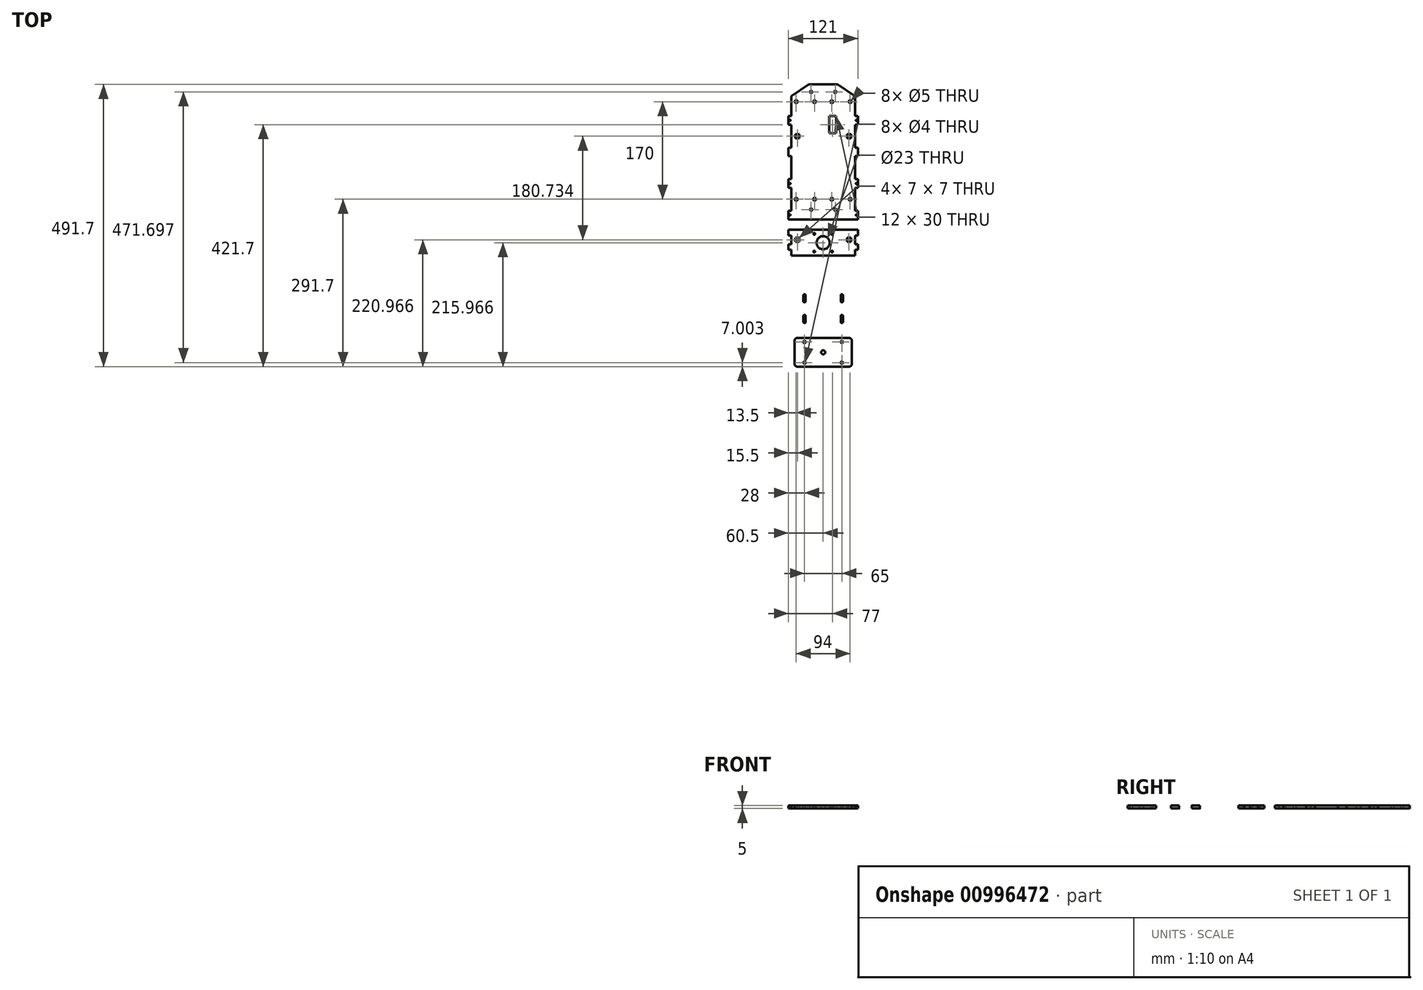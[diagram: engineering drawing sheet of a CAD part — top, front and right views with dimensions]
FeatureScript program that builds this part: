
annotation { "Feature Type Name" : "Feature", "Feature Type Description" : "" }
export const myFeature = defineFeature(function(context is Context, id is Id, definition is map)
    precondition{}
    {
        {
            var Q0;
            Q0=qCreatedBy(makeId("Top.planeOp"),FACE);
            var sketch = newSketch(context, id + "F0", { "sketchPlane" : qUnion([Q0])});
            skLineSegment(sketch, "E0.bottom", {"start": v(-55.5, 107.5) * mm, "end": v(55.5, 107.5) * mm, "construction": true});
            skLineSegment(sketch, "E0.top", {"start": v(-55.5, -107.5) * mm, "end": v(55.5, -107.5) * mm});
            skLineSegment(sketch, "E0.left", {"start": v(-55.5, 107.5) * mm, "end": v(-55.5, 72.5) * mm});
            skLineSegment(sketch, "E0.right", {"start": v(55.5, 107.5) * mm, "end": v(55.5, 72.5) * mm});
            skLineSegment(sketch, "E1", {"start": v(-55.5, 0) * mm, "end": v(55.5, 0) * mm, "construction": true});
            skLineSegment(sketch, "E2", {"start": v(0, 107.5) * mm, "end": v(0, -107.5) * mm, "construction": true});
            skLineSegment(sketch, "E3", {"start": v(-55.5, 107.5) * mm, "end": v(-25.5, 127.5) * mm});
            skLineSegment(sketch, "E4", {"start": v(-25.5, 127.5) * mm, "end": v(25.5, 127.5) * mm});
            skLineSegment(sketch, "E5", {"start": v(25.5, 127.5) * mm, "end": v(55.5, 107.5) * mm});
            skLineSegment(sketch, "E6.bottom", {"start": v(-55.5, -107.5) * mm, "end": v(-60.5, -107.5) * mm});
            skLineSegment(sketch, "E6.top", {"start": v(-55.5, -92.5) * mm, "end": v(-60.5, -92.5) * mm});
            skLineSegment(sketch, "E6.right", {"start": v(-60.5, -107.5) * mm, "end": v(-60.5, -92.5) * mm});
            skLineSegment(sketch, "E7.MirrorCS", {"start": v(55.5, -92.5) * mm, "end": v(60.5, -92.5) * mm});
            skLineSegment(sketch, "E8.MirrorCS", {"start": v(60.5, -107.5) * mm, "end": v(60.5, -92.5) * mm});
            skLineSegment(sketch, "E9.MirrorCS", {"start": v(55.5, -107.5) * mm, "end": v(60.5, -107.5) * mm});
            skLineSegment(sketch, "E10.bottom", {"start": v(-55.5, -52.5) * mm, "end": v(-60.5, -52.5) * mm});
            skLineSegment(sketch, "E10.top", {"start": v(-55.5, -37.5) * mm, "end": v(-60.5, -37.5) * mm});
            skLineSegment(sketch, "E10.right", {"start": v(-60.5, -52.5) * mm, "end": v(-60.5, -37.5) * mm});
            skLineSegment(sketch, "E11.bottom", {"start": v(-55.5, 2.5) * mm, "end": v(-60.5, 2.5) * mm});
            skLineSegment(sketch, "E11.top", {"start": v(-55.5, 17.5) * mm, "end": v(-60.5, 17.5) * mm});
            skLineSegment(sketch, "E11.right", {"start": v(-60.5, 2.5) * mm, "end": v(-60.5, 17.5) * mm});
            skLineSegment(sketch, "E12.bottom", {"start": v(-55.5, 57.5) * mm, "end": v(-60.5, 57.5) * mm});
            skLineSegment(sketch, "E12.top", {"start": v(-55.5, 72.5) * mm, "end": v(-60.5, 72.5) * mm});
            skLineSegment(sketch, "E12.right", {"start": v(-60.5, 57.5) * mm, "end": v(-60.5, 72.5) * mm});
            skLineSegment(sketch, "E13.MirrorCS", {"start": v(55.5, 72.5) * mm, "end": v(60.5, 72.5) * mm});
            skLineSegment(sketch, "E14.MirrorCS", {"start": v(60.5, 57.5) * mm, "end": v(60.5, 72.5) * mm});
            skLineSegment(sketch, "E15.MirrorCS", {"start": v(55.5, 57.5) * mm, "end": v(60.5, 57.5) * mm});
            skLineSegment(sketch, "E16.MirrorCS", {"start": v(55.5, 17.5) * mm, "end": v(60.5, 17.5) * mm});
            skLineSegment(sketch, "E17.MirrorCS", {"start": v(60.5, 2.5) * mm, "end": v(60.5, 17.5) * mm});
            skLineSegment(sketch, "E18.MirrorCS", {"start": v(55.5, 2.5) * mm, "end": v(60.5, 2.5) * mm});
            skLineSegment(sketch, "E19.MirrorCS", {"start": v(55.5, -37.5) * mm, "end": v(60.5, -37.5) * mm});
            skLineSegment(sketch, "E20.MirrorCS", {"start": v(60.5, -52.5) * mm, "end": v(60.5, -37.5) * mm});
            skLineSegment(sketch, "E21.MirrorCS", {"start": v(55.5, -52.5) * mm, "end": v(60.5, -52.5) * mm});
            skLineSegment(sketch, "E22.trimOffspring", {"start": v(55.5, 57.5) * mm, "end": v(55.5, 17.5) * mm});
            skLineSegment(sketch, "E23.trimOffspring", {"start": v(55.5, 2.5) * mm, "end": v(55.5, -37.5) * mm});
            skLineSegment(sketch, "E24.trimOffspring", {"start": v(55.5, -52.5) * mm, "end": v(55.5, -92.5) * mm});
            skLineSegment(sketch, "E25.trimOffspring", {"start": v(-55.5, -52.5) * mm, "end": v(-55.5, -92.5) * mm});
            skLineSegment(sketch, "E26.trimOffspring", {"start": v(-55.5, 2.5) * mm, "end": v(-55.5, -37.5) * mm});
            skLineSegment(sketch, "E27.trimOffspring", {"start": v(-55.5, 57.5) * mm, "end": v(-55.5, 17.5) * mm});
            skLineSegment(sketch, "E28.bottom", {"start": v(10.5, 72.5) * mm, "end": v(22.5, 72.5) * mm});
            skLineSegment(sketch, "E28.top", {"start": v(10.5, 42.5) * mm, "end": v(22.5, 42.5) * mm});
            skLineSegment(sketch, "E28.left", {"start": v(10.5, 72.5) * mm, "end": v(10.5, 42.5) * mm});
            skLineSegment(sketch, "E28.right", {"start": v(22.5, 72.5) * mm, "end": v(22.5, 42.5) * mm});
            skLineSegment(sketch, "E29.bottom", {"start": v(-48.5, 41) * mm, "end": v(-41.5, 41) * mm});
            skLineSegment(sketch, "E29.top", {"start": v(-48.5, 34) * mm, "end": v(-41.5, 34) * mm});
            skLineSegment(sketch, "E29.left", {"start": v(-48.5, 41) * mm, "end": v(-48.5, 34) * mm});
            skLineSegment(sketch, "E29.right", {"start": v(-41.5, 41) * mm, "end": v(-41.5, 34) * mm});
            skPoint(sketch, "E30", {"position": v(-48.5, 37.5) * mm});
            skPoint(sketch, "E31", {"position": v(-55.5, 37.5) * mm});
            skLineSegment(sketch, "E32.MirrorCS", {"start": v(41.5, 41) * mm, "end": v(41.5, 34) * mm});
            skLineSegment(sketch, "E33.MirrorCS", {"start": v(48.5, 41) * mm, "end": v(41.5, 41) * mm});
            skLineSegment(sketch, "E34.MirrorCS", {"start": v(48.5, 41) * mm, "end": v(48.5, 34) * mm});
            skLineSegment(sketch, "E35.MirrorCS", {"start": v(48.5, 34) * mm, "end": v(41.5, 34) * mm});
            skSolve(sketch);
        }
        {
            var Q0;
            Q0=makeQuery(id+"F0.imprint","IMPRINT",FACE,{"disambiguationData":[TD([[makeQuery(id+"F0.imprint","IMPRINT",EDGE,{"derivedFrom":sQuery(id+"F0.wireOp",EDGE,"E0.top")}),1.0]])]});
            extrude(context, id + "F1", {"entities" : qUnion([Q0]), "depth" : 5 * mm, "offsetDistance" : 25 * mm});
        }
        {
            var Q0;
            Q0=makeQuery(id+"F1.opExtrude","CAP_FACE",FACE,{"disambiguationData":[OSD([sQuery(id+"F0.wireOp",EDGE,"E0.bottom"),sQuery(id+"F0.wireOp",EDGE,"E0.top"),sQuery(id+"F0.wireOp",EDGE,"E0.left"),sQuery(id+"F0.wireOp",EDGE,"E0.right")])],"isStart":false});
            var sketch = newSketch(context, id + "F2", { "sketchPlane" : qUnion([Q0])});
            skPoint(sketch, "E36", {"position": v(-47, 97.5) * mm});
            skPoint(sketch, "E37", {"position": v(-15, 97.5) * mm});
            skPoint(sketch, "E38", {"position": v(-47, -72.5) * mm});
            skPoint(sketch, "E39", {"position": v(-15, -72.5) * mm});
            skLineSegment(sketch, "E40.bottom", {"start": v(-55.5, 107.5) * mm, "end": v(55.5, 107.5) * mm});
            skLineSegment(sketch, "E40.top", {"start": v(-55.5, 107.5) * mm, "end": v(55.5, 107.5) * mm});
            skLineSegment(sketch, "E40.left", {"start": v(-55.5, 107.5) * mm, "end": v(-55.5, 107.5) * mm});
            skLineSegment(sketch, "E40.right", {"start": v(55.5, 107.5) * mm, "end": v(55.5, 107.5) * mm});
            skLineSegment(sketch, "E41", {"start": v(0, 107.5) * mm, "end": v(0, 107.5) * mm});
            skPoint(sketch, "E42", {"position": v(15, 97.5) * mm});
            skPoint(sketch, "E43", {"position": v(47, 97.5) * mm});
            skPoint(sketch, "E44", {"position": v(47, -72.5) * mm});
            skPoint(sketch, "E45", {"position": v(15, -72.5) * mm});
            skLineSegment(sketch, "E46", {"start": v(-47, 97.5) * mm, "end": v(-15, 97.5) * mm, "construction": true});
            skLineSegment(sketch, "E47", {"start": v(15, 97.5) * mm, "end": v(47, 97.5) * mm, "construction": true});
            skPoint(sketch, "E48", {"position": v(-31, 97.5) * mm});
            skPoint(sketch, "E49", {"position": v(31, 97.5) * mm});
            skSolve(sketch);
        }
        {
            var Q0;
            Q0=sQuery(id+"F2.wireOp",VERTEX,"E36");
            var Q1;
            Q1=sQuery(id+"F2.wireOp",VERTEX,"E37");
            var Q2;
            Q2=sQuery(id+"F2.wireOp",VERTEX,"E42");
            var Q3;
            Q3=sQuery(id+"F2.wireOp",VERTEX,"E43");
            var Q4;
            Q4=sQuery(id+"F2.wireOp",VERTEX,"E44");
            var Q5;
            Q5=sQuery(id+"F2.wireOp",VERTEX,"E45");
            var Q6;
            Q6=sQuery(id+"F2.wireOp",VERTEX,"E39");
            var Q7;
            Q7=sQuery(id+"F2.wireOp",VERTEX,"E38");
            var Q8;
            Q8=makeQuery(id+"F1.opExtrude","SWEPT_BODY",BODY,{"disambiguationData":[OSD([sQuery(id+"F0.wireOp",EDGE,"E0.top"),sQuery(id+"F0.wireOp",EDGE,"E0.left"),sQuery(id+"F0.wireOp",EDGE,"E0.right"),sQuery(id+"F0.wireOp",EDGE,"E3"),sQuery(id+"F0.wireOp",EDGE,"E4"),sQuery(id+"F0.wireOp",EDGE,"E5")])]});
            hole(context, id + "F3", {"style" : HoleStyle.SIMPLE, "endStyle" : HoleEndStyle.THROUGH, "holeDiameter" : 5 * mm, "majorDiameter" : 5 * mm, "isTappedThrough" : true, "tappedDepth" : 12 * mm, "tapClearance" : 3, "locations" : qUnion([Q0, Q1, Q2, Q3, Q4, Q5, Q6, Q7]), "scope" : qUnion([Q8])});
        }
        {
            var Q0;
            Q0=makeQuery(id+"F1.opExtrude","SWEPT_EDGE",EDGE,{"disambiguationData":[OSD([sQuery(id+"F0.wireOp",EDGE,"E0.left"),sQuery(id+"F0.wireOp",EDGE,"E3")])]});
            var Q1;
            Q1=makeQuery(id+"F1.opExtrude","SWEPT_EDGE",EDGE,{"disambiguationData":[OSD([sQuery(id+"F0.wireOp",EDGE,"E3"),sQuery(id+"F0.wireOp",EDGE,"E4")])]});
            var Q2;
            Q2=makeQuery(id+"F1.opExtrude","SWEPT_EDGE",EDGE,{"disambiguationData":[OSD([sQuery(id+"F0.wireOp",EDGE,"E4"),sQuery(id+"F0.wireOp",EDGE,"E5")])]});
            var Q3;
            Q3=makeQuery(id+"F1.opExtrude","SWEPT_EDGE",EDGE,{"disambiguationData":[OSD([sQuery(id+"F0.wireOp",EDGE,"E0.right"),sQuery(id+"F0.wireOp",EDGE,"E5")])]});
            fillet(context, id + "F4", {"entities" : qUnion([Q0, Q1, Q2, Q3]), "radius" : 5 * mm, "tangentPropagation" : true, "allowEdgeOverflow" : false});
        }
        {
            var Q0;
            Q0=makeQuery(id+"F1.opExtrude","CAP_FACE",FACE,{"disambiguationData":[OSD([sQuery(id+"F0.wireOp",EDGE,"E0.top"),sQuery(id+"F0.wireOp",EDGE,"E0.left"),sQuery(id+"F0.wireOp",EDGE,"E0.right"),sQuery(id+"F0.wireOp",EDGE,"E3"),sQuery(id+"F0.wireOp",EDGE,"E4"),sQuery(id+"F0.wireOp",EDGE,"E5")])],"isStart":false});
            var sketch = newSketch(context, id + "F5", { "sketchPlane" : qUnion([Q0])});
            skLineSegment(sketch, "E50", {"start": v(0, -107.5) * mm, "end": v(0, 127.5) * mm, "construction": true});
            skPoint(sketch, "E51", {"position": v(-21, 114.5) * mm});
            skPoint(sketch, "E52", {"position": v(21, 114.5) * mm});
            skPoint(sketch, "E53", {"position": v(-21, -90.5) * mm});
            skPoint(sketch, "E54", {"position": v(21, -90.5) * mm});
            skSolve(sketch);
        }
        {
            var Q0;
            Q0=sQuery(id+"F5.wireOp",VERTEX,"E51");
            var Q1;
            Q1=sQuery(id+"F5.wireOp",VERTEX,"E52");
            var Q2;
            Q2=sQuery(id+"F5.wireOp",VERTEX,"E53");
            var Q3;
            Q3=sQuery(id+"F5.wireOp",VERTEX,"E54");
            var Q4;
            Q4=makeQuery(id+"F1.opExtrude","SWEPT_BODY",BODY,{"disambiguationData":[OSD([sQuery(id+"F0.wireOp",EDGE,"E0.top"),sQuery(id+"F0.wireOp",EDGE,"E0.left"),sQuery(id+"F0.wireOp",EDGE,"E0.right"),sQuery(id+"F0.wireOp",EDGE,"E3"),sQuery(id+"F0.wireOp",EDGE,"E4"),sQuery(id+"F0.wireOp",EDGE,"E5")])]});
            hole(context, id + "F6", {"style" : HoleStyle.SIMPLE, "endStyle" : HoleEndStyle.THROUGH, "holeDiameter" : 4 * mm, "majorDiameter" : 5 * mm, "isTappedThrough" : true, "tappedDepth" : 12 * mm, "tapClearance" : 3, "locations" : qUnion([Q0, Q1, Q2, Q3]), "scope" : qUnion([Q4])});
        }
        {
            var Q0;
            Q0=qCreatedBy(makeId("Top.planeOp"),FACE);
            var sketch = newSketch(context, id + "F7", { "sketchPlane" : qUnion([Q0])});
            skLineSegment(sketch, "E55.bottom", {"start": v(-55.5, -125.73) * mm, "end": v(55.5, -125.73) * mm});
            skLineSegment(sketch, "E55.top", {"start": v(-55.5, -170.73) * mm, "end": v(55.5, -170.73) * mm});
            skLineSegment(sketch, "E55.left", {"start": v(-55.5, -135.73) * mm, "end": v(-55.5, -150.73) * mm});
            skLineSegment(sketch, "E55.right", {"start": v(55.5, -135.73) * mm, "end": v(55.5, -150.73) * mm});
            skPoint(sketch, "E56", {"position": v(0, -125.73) * mm});
            skLineSegment(sketch, "E57", {"start": v(0, -109.47) * mm, "end": v(0, -207.16) * mm, "construction": true});
            skLineSegment(sketch, "E58.bottom", {"start": v(-55.5, -160.73) * mm, "end": v(-60.5, -160.73) * mm});
            skLineSegment(sketch, "E58.top", {"start": v(-55.5, -150.73) * mm, "end": v(-60.5, -150.73) * mm});
            skLineSegment(sketch, "E58.right", {"start": v(-60.5, -160.73) * mm, "end": v(-60.5, -150.73) * mm});
            skLineSegment(sketch, "E59.bottom", {"start": v(-55.5, -135.73) * mm, "end": v(-60.5, -135.73) * mm});
            skLineSegment(sketch, "E59.top", {"start": v(-55.5, -125.73) * mm, "end": v(-60.5, -125.73) * mm});
            skLineSegment(sketch, "E59.right", {"start": v(-60.5, -135.73) * mm, "end": v(-60.5, -125.73) * mm});
            skLineSegment(sketch, "E60.MirrorCS", {"start": v(55.5, -135.73) * mm, "end": v(60.5, -135.73) * mm});
            skLineSegment(sketch, "E61.MirrorCS", {"start": v(60.5, -135.73) * mm, "end": v(60.5, -125.73) * mm});
            skLineSegment(sketch, "E62.MirrorCS", {"start": v(55.5, -125.73) * mm, "end": v(60.5, -125.73) * mm});
            skLineSegment(sketch, "E63.MirrorCS", {"start": v(55.5, -150.73) * mm, "end": v(60.5, -150.73) * mm});
            skLineSegment(sketch, "E64.MirrorCS", {"start": v(60.5, -160.73) * mm, "end": v(60.5, -150.73) * mm});
            skLineSegment(sketch, "E65.MirrorCS", {"start": v(55.5, -160.73) * mm, "end": v(60.5, -160.73) * mm});
            skLineSegment(sketch, "E66.trimOffspring", {"start": v(-55.5, -160.73) * mm, "end": v(-55.5, -170.73) * mm});
            skLineSegment(sketch, "E67.trimOffspring", {"start": v(55.5, -160.73) * mm, "end": v(55.5, -170.73) * mm});
            skLineSegment(sketch, "E68.bottom", {"start": v(-48.5, -139.73) * mm, "end": v(-41.5, -139.73) * mm});
            skLineSegment(sketch, "E68.top", {"start": v(-48.5, -146.73) * mm, "end": v(-41.5, -146.73) * mm});
            skLineSegment(sketch, "E68.left", {"start": v(-48.5, -139.73) * mm, "end": v(-48.5, -146.73) * mm});
            skLineSegment(sketch, "E68.right", {"start": v(-41.5, -139.73) * mm, "end": v(-41.5, -146.73) * mm});
            skPoint(sketch, "E69", {"position": v(-55.5, -143.23) * mm});
            skPoint(sketch, "E70", {"position": v(-48.5, -143.23) * mm});
            skLineSegment(sketch, "E71.MirrorCS", {"start": v(41.5, -139.73) * mm, "end": v(41.5, -146.73) * mm});
            skLineSegment(sketch, "E72.MirrorCS", {"start": v(48.5, -139.73) * mm, "end": v(41.5, -139.73) * mm});
            skLineSegment(sketch, "E73.MirrorCS", {"start": v(48.5, -139.73) * mm, "end": v(48.5, -146.73) * mm});
            skLineSegment(sketch, "E74.MirrorCS", {"start": v(48.5, -146.73) * mm, "end": v(41.5, -146.73) * mm});
            skSolve(sketch);
        }
        {
            var Q0;
            Q0=makeQuery(id+"F7.imprint","IMPRINT",FACE,{"disambiguationData":[TD([[makeQuery(id+"F7.imprint","IMPRINT",EDGE,{"derivedFrom":sQuery(id+"F7.wireOp",EDGE,"E55.bottom")}),-1.0]])]});
            extrude(context, id + "F8", {"entities" : qUnion([Q0]), "depth" : 5 * mm, "offsetDistance" : 25 * mm});
        }
        {
            var Q0;
            Q0=makeQuery(id+"F8.opExtrude","CAP_FACE",FACE,{"disambiguationData":[OSD([sQuery(id+"F7.wireOp",EDGE,"E55.bottom"),sQuery(id+"F7.wireOp",EDGE,"E55.top"),sQuery(id+"F7.wireOp",EDGE,"E55.left"),sQuery(id+"F7.wireOp",EDGE,"E55.right"),sQuery(id+"F7.wireOp",EDGE,"E58.bottom"),sQuery(id+"F7.wireOp",EDGE,"E58.top"),sQuery(id+"F7.wireOp",EDGE,"E58.right"),sQuery(id+"F7.wireOp",EDGE,"E59.bottom"),sQuery(id+"F7.wireOp",EDGE,"E59.top"),sQuery(id+"F7.wireOp",EDGE,"E59.right"),sQuery(id+"F7.wireOp",EDGE,"E60.MirrorCS"),sQuery(id+"F7.wireOp",EDGE,"E61.MirrorCS"),sQuery(id+"F7.wireOp",EDGE,"E62.MirrorCS"),sQuery(id+"F7.wireOp",EDGE,"E63.MirrorCS"),sQuery(id+"F7.wireOp",EDGE,"E64.MirrorCS"),sQuery(id+"F7.wireOp",EDGE,"E65.MirrorCS"),sQuery(id+"F7.wireOp",EDGE,"E66.trimOffspring"),sQuery(id+"F7.wireOp",EDGE,"E67.trimOffspring")])],"isStart":false});
            var sketch = newSketch(context, id + "F9", { "sketchPlane" : qUnion([Q0])});
            skLineSegment(sketch, "E75", {"start": v(0, -125.73) * mm, "end": v(0, -170.73) * mm, "construction": true});
            skLineSegment(sketch, "E76", {"start": v(-48.92, -148.23) * mm, "end": v(50.75, -148.23) * mm, "construction": true});
            skPoint(sketch, "E76.startSnap0", {"position": v(0, -148.23) * mm});
            skPoint(sketch, "E77", {"position": v(-15.5, -132.73) * mm});
            skPoint(sketch, "E78", {"position": v(15.5, -132.73) * mm});
            skPoint(sketch, "E79", {"position": v(15.5, -163.73) * mm});
            skPoint(sketch, "E80", {"position": v(-15.5, -163.73) * mm});
            skSolve(sketch);
        }
        {
            var Q0;
            Q0=sQuery(id+"F9.wireOp",VERTEX,"E77");
            var Q1;
            Q1=sQuery(id+"F9.wireOp",VERTEX,"E78");
            var Q2;
            Q2=sQuery(id+"F9.wireOp",VERTEX,"E79");
            var Q3;
            Q3=sQuery(id+"F9.wireOp",VERTEX,"E80");
            var Q4;
            Q4=makeQuery(id+"F8.opExtrude","SWEPT_BODY",BODY,{"disambiguationData":[OSD([sQuery(id+"F7.wireOp",EDGE,"E55.bottom"),sQuery(id+"F7.wireOp",EDGE,"E55.top"),sQuery(id+"F7.wireOp",EDGE,"E55.left"),sQuery(id+"F7.wireOp",EDGE,"E55.right"),sQuery(id+"F7.wireOp",EDGE,"E58.bottom"),sQuery(id+"F7.wireOp",EDGE,"E58.top"),sQuery(id+"F7.wireOp",EDGE,"E58.right"),sQuery(id+"F7.wireOp",EDGE,"E59.bottom"),sQuery(id+"F7.wireOp",EDGE,"E59.top"),sQuery(id+"F7.wireOp",EDGE,"E59.right"),sQuery(id+"F7.wireOp",EDGE,"E60.MirrorCS"),sQuery(id+"F7.wireOp",EDGE,"E61.MirrorCS"),sQuery(id+"F7.wireOp",EDGE,"E62.MirrorCS"),sQuery(id+"F7.wireOp",EDGE,"E63.MirrorCS"),sQuery(id+"F7.wireOp",EDGE,"E64.MirrorCS"),sQuery(id+"F7.wireOp",EDGE,"E65.MirrorCS"),sQuery(id+"F7.wireOp",EDGE,"E66.trimOffspring"),sQuery(id+"F7.wireOp",EDGE,"E67.trimOffspring")])]});
            hole(context, id + "F10", {"style" : HoleStyle.SIMPLE, "endStyle" : HoleEndStyle.THROUGH, "holeDiameter" : 3 * mm, "majorDiameter" : 5 * mm, "isTappedThrough" : true, "tappedDepth" : 12 * mm, "tapClearance" : 3, "locations" : qUnion([Q0, Q1, Q2, Q3]), "scope" : qUnion([Q4])});
        }
        {
            var Q0;
            Q0=makeQuery(id+"F8.opExtrude","CAP_FACE",FACE,{"disambiguationData":[OSD([sQuery(id+"F7.wireOp",EDGE,"E55.bottom"),sQuery(id+"F7.wireOp",EDGE,"E55.top"),sQuery(id+"F7.wireOp",EDGE,"E55.left"),sQuery(id+"F7.wireOp",EDGE,"E55.right"),sQuery(id+"F7.wireOp",EDGE,"E58.bottom"),sQuery(id+"F7.wireOp",EDGE,"E58.top"),sQuery(id+"F7.wireOp",EDGE,"E58.right"),sQuery(id+"F7.wireOp",EDGE,"E59.bottom"),sQuery(id+"F7.wireOp",EDGE,"E59.top"),sQuery(id+"F7.wireOp",EDGE,"E59.right"),sQuery(id+"F7.wireOp",EDGE,"E60.MirrorCS"),sQuery(id+"F7.wireOp",EDGE,"E61.MirrorCS"),sQuery(id+"F7.wireOp",EDGE,"E62.MirrorCS"),sQuery(id+"F7.wireOp",EDGE,"E63.MirrorCS"),sQuery(id+"F7.wireOp",EDGE,"E64.MirrorCS"),sQuery(id+"F7.wireOp",EDGE,"E65.MirrorCS"),sQuery(id+"F7.wireOp",EDGE,"E66.trimOffspring"),sQuery(id+"F7.wireOp",EDGE,"E67.trimOffspring")])],"isStart":false});
            var sketch = newSketch(context, id + "F11", { "sketchPlane" : qUnion([Q0])});
            skLineSegment(sketch, "E81", {"start": v(0, -125.73) * mm, "end": v(0, -170.73) * mm, "construction": true});
            skPoint(sketch, "E82", {"position": v(0, -148.23) * mm});
            skSolve(sketch);
        }
        {
            var Q0;
            Q0=sQuery(id+"F11.wireOp",VERTEX,"E82");
            var Q1;
            Q1=makeQuery(id+"F8.opExtrude","SWEPT_BODY",BODY,{"disambiguationData":[OSD([sQuery(id+"F7.wireOp",EDGE,"E55.bottom"),sQuery(id+"F7.wireOp",EDGE,"E55.top"),sQuery(id+"F7.wireOp",EDGE,"E55.left"),sQuery(id+"F7.wireOp",EDGE,"E55.right"),sQuery(id+"F7.wireOp",EDGE,"E58.bottom"),sQuery(id+"F7.wireOp",EDGE,"E58.top"),sQuery(id+"F7.wireOp",EDGE,"E58.right"),sQuery(id+"F7.wireOp",EDGE,"E59.bottom"),sQuery(id+"F7.wireOp",EDGE,"E59.top"),sQuery(id+"F7.wireOp",EDGE,"E59.right"),sQuery(id+"F7.wireOp",EDGE,"E60.MirrorCS"),sQuery(id+"F7.wireOp",EDGE,"E61.MirrorCS"),sQuery(id+"F7.wireOp",EDGE,"E62.MirrorCS"),sQuery(id+"F7.wireOp",EDGE,"E63.MirrorCS"),sQuery(id+"F7.wireOp",EDGE,"E64.MirrorCS"),sQuery(id+"F7.wireOp",EDGE,"E65.MirrorCS"),sQuery(id+"F7.wireOp",EDGE,"E66.trimOffspring"),sQuery(id+"F7.wireOp",EDGE,"E67.trimOffspring")])]});
            hole(context, id + "F12", {"style" : HoleStyle.SIMPLE, "endStyle" : HoleEndStyle.THROUGH, "holeDiameter" : 23 * mm, "majorDiameter" : 6.35 * mm, "isTappedThrough" : true, "tappedDepth" : 12 * mm, "tapClearance" : 3, "locations" : qUnion([Q0]), "scope" : qUnion([Q1])});
        }
        {
            var Q0;
            Q0=qCreatedBy(makeId("Top.planeOp"),FACE);
            var sketch = newSketch(context, id + "F13", { "sketchPlane" : qUnion([Q0])});
            skLineSegment(sketch, "E83", {"start": v(0, 0) * mm, "end": v(0, -291.14) * mm, "construction": true});
            skLineSegment(sketch, "E84.bottom", {"start": v(-55.5, -188.16) * mm, "end": v(-32, -188.16) * mm});
            skLineSegment(sketch, "E84.top", {"start": v(-55.5, -277.16) * mm, "end": v(55.5, -277.16) * mm, "construction": true});
            skLineSegment(sketch, "E84.left", {"start": v(-55.5, -188.16) * mm, "end": v(-55.5, -197.16) * mm});
            skLineSegment(sketch, "E84.right", {"start": v(55.5, -188.16) * mm, "end": v(55.5, -197.16) * mm});
            skLineSegment(sketch, "E85", {"start": v(-78.24, -232.66) * mm, "end": v(84.2, -232.66) * mm, "construction": true});
            skLineSegment(sketch, "E86.bottom", {"start": v(-55.5, -262.16) * mm, "end": v(-60.5, -262.16) * mm});
            skLineSegment(sketch, "E86.top", {"start": v(-55.5, -252.16) * mm, "end": v(-60.5, -252.16) * mm});
            skLineSegment(sketch, "E86.right", {"start": v(-60.5, -262.16) * mm, "end": v(-60.5, -252.16) * mm});
            skLineSegment(sketch, "E87.bottom", {"start": v(-55.5, -237.16) * mm, "end": v(-60.5, -237.16) * mm});
            skLineSegment(sketch, "E87.top", {"start": v(-55.5, -227.16) * mm, "end": v(-60.5, -227.16) * mm});
            skLineSegment(sketch, "E87.right", {"start": v(-60.5, -237.16) * mm, "end": v(-60.5, -227.16) * mm});
            skLineSegment(sketch, "E88.bottom", {"start": v(-55.5, -207.16) * mm, "end": v(-60.5, -207.16) * mm});
            skLineSegment(sketch, "E88.top", {"start": v(-55.5, -197.16) * mm, "end": v(-60.5, -197.16) * mm});
            skLineSegment(sketch, "E88.right", {"start": v(-60.5, -207.16) * mm, "end": v(-60.5, -197.16) * mm});
            skLineSegment(sketch, "E89.MirrorCS", {"start": v(55.5, -197.16) * mm, "end": v(60.5, -197.16) * mm});
            skLineSegment(sketch, "E90.MirrorCS", {"start": v(60.5, -207.16) * mm, "end": v(60.5, -197.16) * mm});
            skLineSegment(sketch, "E91.MirrorCS", {"start": v(55.5, -207.16) * mm, "end": v(60.5, -207.16) * mm});
            skLineSegment(sketch, "E92.MirrorCS", {"start": v(55.5, -252.16) * mm, "end": v(60.5, -252.16) * mm});
            skLineSegment(sketch, "E93.MirrorCS", {"start": v(60.5, -262.16) * mm, "end": v(60.5, -252.16) * mm});
            skLineSegment(sketch, "E94.MirrorCS", {"start": v(55.5, -262.16) * mm, "end": v(60.5, -262.16) * mm});
            skLineSegment(sketch, "E95.MirrorCS", {"start": v(60.5, -237.16) * mm, "end": v(60.5, -227.16) * mm});
            skLineSegment(sketch, "E96.MirrorCS", {"start": v(55.5, -237.16) * mm, "end": v(60.5, -237.16) * mm});
            skLineSegment(sketch, "E97.MirrorCS", {"start": v(55.5, -227.16) * mm, "end": v(60.5, -227.16) * mm});
            skLineSegment(sketch, "E98.trimOffspring", {"start": v(-55.5, -207.16) * mm, "end": v(-55.5, -227.16) * mm});
            skLineSegment(sketch, "E99.trimOffspring", {"start": v(55.5, -207.16) * mm, "end": v(55.5, -227.16) * mm});
            skLineSegment(sketch, "E100.trimOffspring", {"start": v(55.5, -237.16) * mm, "end": v(55.5, -252.16) * mm});
            skLineSegment(sketch, "E101.trimOffspring", {"start": v(-55.5, -237.16) * mm, "end": v(-55.5, -252.16) * mm});
            skLineSegment(sketch, "E102.trimOffspring", {"start": v(-55.5, -262.16) * mm, "end": v(-55.5, -277.16) * mm});
            skLineSegment(sketch, "E103.trimOffspring", {"start": v(55.5, -262.16) * mm, "end": v(55.5, -277.16) * mm});
            skLineSegment(sketch, "E104", {"start": v(-32, -188.16) * mm, "end": v(-32, -201.16) * mm});
            skLineSegment(sketch, "E105", {"start": v(-32, -201.16) * mm, "end": v(-18.5, -220.16) * mm});
            skLineSegment(sketch, "E106", {"start": v(-18.5, -220.16) * mm, "end": v(0, -220.16) * mm});
            skLineSegment(sketch, "E107.MirrorCS", {"start": v(18.5, -220.16) * mm, "end": v(0, -220.16) * mm});
            skLineSegment(sketch, "E108.MirrorCS", {"start": v(32, -201.16) * mm, "end": v(18.5, -220.16) * mm});
            skLineSegment(sketch, "E109.MirrorCS", {"start": v(32, -188.16) * mm, "end": v(32, -201.16) * mm});
            skLineSegment(sketch, "E110.trimOffspring", {"start": v(32, -188.16) * mm, "end": v(55.5, -188.16) * mm});
            skLineSegment(sketch, "E111.top", {"start": v(-55.5, -293.16) * mm, "end": v(55.5, -293.16) * mm});
            skLineSegment(sketch, "E111.left", {"start": v(-55.5, -277.16) * mm, "end": v(-55.5, -293.16) * mm});
            skLineSegment(sketch, "E111.right", {"start": v(55.5, -277.16) * mm, "end": v(55.5, -293.16) * mm});
            skLineSegment(sketch, "E112.bottom", {"start": v(-48.5, -213.66) * mm, "end": v(-41.5, -213.66) * mm});
            skLineSegment(sketch, "E112.top", {"start": v(-48.5, -220.66) * mm, "end": v(-41.5, -220.66) * mm});
            skLineSegment(sketch, "E112.left", {"start": v(-48.5, -213.66) * mm, "end": v(-48.5, -220.66) * mm});
            skLineSegment(sketch, "E112.right", {"start": v(-41.5, -213.66) * mm, "end": v(-41.5, -220.66) * mm});
            skPoint(sketch, "E113", {"position": v(-48.5, -217.16) * mm});
            skPoint(sketch, "E114", {"position": v(-55.5, -217.16) * mm});
            skLineSegment(sketch, "E115.MirrorCS", {"start": v(48.5, -213.66) * mm, "end": v(41.5, -213.66) * mm});
            skLineSegment(sketch, "E116.MirrorCS", {"start": v(48.5, -213.66) * mm, "end": v(48.5, -220.66) * mm});
            skLineSegment(sketch, "E117.MirrorCS", {"start": v(41.5, -213.66) * mm, "end": v(41.5, -220.66) * mm});
            skLineSegment(sketch, "E118.MirrorCS", {"start": v(48.5, -220.66) * mm, "end": v(41.5, -220.66) * mm});
            skLineSegment(sketch, "E119.bottom", {"start": v(-48.5, -241.16) * mm, "end": v(-41.5, -241.16) * mm});
            skLineSegment(sketch, "E119.top", {"start": v(-48.5, -248.16) * mm, "end": v(-41.5, -248.16) * mm});
            skLineSegment(sketch, "E119.left", {"start": v(-48.5, -241.16) * mm, "end": v(-48.5, -248.16) * mm});
            skLineSegment(sketch, "E119.right", {"start": v(-41.5, -241.16) * mm, "end": v(-41.5, -248.16) * mm});
            skPoint(sketch, "E120", {"position": v(-48.5, -244.66) * mm});
            skPoint(sketch, "E121", {"position": v(-55.5, -244.66) * mm});
            skLineSegment(sketch, "E122.MirrorCS", {"start": v(48.5, -248.16) * mm, "end": v(41.5, -248.16) * mm});
            skLineSegment(sketch, "E123.MirrorCS", {"start": v(41.5, -241.16) * mm, "end": v(41.5, -248.16) * mm});
            skLineSegment(sketch, "E124.MirrorCS", {"start": v(48.5, -241.16) * mm, "end": v(41.5, -241.16) * mm});
            skLineSegment(sketch, "E125.MirrorCS", {"start": v(48.5, -241.16) * mm, "end": v(48.5, -248.16) * mm});
            skSolve(sketch);
        }
        {
            var Q0;
            Q0=makeQuery(id+"F13.imprint","IMPRINT",FACE,{"disambiguationData":[TD([[makeQuery(id+"F13.imprint","IMPRINT",EDGE,{"derivedFrom":sQuery(id+"F13.wireOp",EDGE,"E84.bottom")}),-1.0]])]});
            extrude(context, id + "F14", {"entities" : qUnion([Q0]), "depth" : 5 * mm, "offsetDistance" : 25 * mm});
        }
        {
            var Q0;
            Q0=makeQuery(id+"F14.opExtrude","SWEPT_EDGE",EDGE,{"disambiguationData":[OSD([sQuery(id+"F13.wireOp",EDGE,"E108.MirrorCS"),sQuery(id+"F13.wireOp",EDGE,"E109.MirrorCS")])]});
            var Q1;
            Q1=makeQuery(id+"F14.opExtrude","SWEPT_EDGE",EDGE,{"disambiguationData":[OSD([sQuery(id+"F13.wireOp",EDGE,"E107.MirrorCS"),sQuery(id+"F13.wireOp",EDGE,"E108.MirrorCS")])]});
            var Q2;
            Q2=makeQuery(id+"F14.opExtrude","SWEPT_EDGE",EDGE,{"disambiguationData":[OSD([sQuery(id+"F13.wireOp",EDGE,"E105"),sQuery(id+"F13.wireOp",EDGE,"E106")])]});
            var Q3;
            Q3=makeQuery(id+"F14.opExtrude","SWEPT_EDGE",EDGE,{"disambiguationData":[OSD([sQuery(id+"F13.wireOp",EDGE,"E104"),sQuery(id+"F13.wireOp",EDGE,"E105")])]});
            var Q4;
            Q4=makeQuery(id+"F14.opExtrude","SWEPT_EDGE",EDGE,{"disambiguationData":[OSD([sQuery(id+"F13.wireOp",EDGE,"E111.top"),sQuery(id+"F13.wireOp",EDGE,"E111.left")])]});
            var Q5;
            Q5=makeQuery(id+"F14.opExtrude","SWEPT_EDGE",EDGE,{"disambiguationData":[OSD([sQuery(id+"F13.wireOp",EDGE,"E111.top"),sQuery(id+"F13.wireOp",EDGE,"E111.right")])]});
            fillet(context, id + "F15", {"entities" : qUnion([Q0, Q1, Q2, Q3, Q4, Q5]), "radius" : 10 * mm, "tangentPropagation" : true, "allowEdgeOverflow" : false});
        }
        {
            var Q0;
            Q0=makeQuery(id+"F14.opExtrude","CAP_FACE",FACE,{"disambiguationData":[OSD([sQuery(id+"F13.wireOp",EDGE,"E84.bottom"),sQuery(id+"F13.wireOp",EDGE,"E84.left"),sQuery(id+"F13.wireOp",EDGE,"E84.right"),sQuery(id+"F13.wireOp",EDGE,"E86.bottom"),sQuery(id+"F13.wireOp",EDGE,"E86.top"),sQuery(id+"F13.wireOp",EDGE,"E86.right"),sQuery(id+"F13.wireOp",EDGE,"E87.bottom"),sQuery(id+"F13.wireOp",EDGE,"E87.top"),sQuery(id+"F13.wireOp",EDGE,"E87.right"),sQuery(id+"F13.wireOp",EDGE,"E88.bottom"),sQuery(id+"F13.wireOp",EDGE,"E88.top"),sQuery(id+"F13.wireOp",EDGE,"E88.right"),sQuery(id+"F13.wireOp",EDGE,"E89.MirrorCS"),sQuery(id+"F13.wireOp",EDGE,"E90.MirrorCS"),sQuery(id+"F13.wireOp",EDGE,"E91.MirrorCS"),sQuery(id+"F13.wireOp",EDGE,"E92.MirrorCS"),sQuery(id+"F13.wireOp",EDGE,"E93.MirrorCS"),sQuery(id+"F13.wireOp",EDGE,"E94.MirrorCS"),sQuery(id+"F13.wireOp",EDGE,"E95.MirrorCS"),sQuery(id+"F13.wireOp",EDGE,"E96.MirrorCS"),sQuery(id+"F13.wireOp",EDGE,"E97.MirrorCS"),sQuery(id+"F13.wireOp",EDGE,"E98.trimOffspring"),sQuery(id+"F13.wireOp",EDGE,"E99.trimOffspring"),sQuery(id+"F13.wireOp",EDGE,"E100.trimOffspring"),sQuery(id+"F13.wireOp",EDGE,"E101.trimOffspring"),sQuery(id+"F13.wireOp",EDGE,"E102.trimOffspring"),sQuery(id+"F13.wireOp",EDGE,"E103.trimOffspring"),sQuery(id+"F13.wireOp",EDGE,"E104"),sQuery(id+"F13.wireOp",EDGE,"E105"),sQuery(id+"F13.wireOp",EDGE,"E106"),sQuery(id+"F13.wireOp",EDGE,"E107.MirrorCS"),sQuery(id+"F13.wireOp",EDGE,"E108.MirrorCS"),sQuery(id+"F13.wireOp",EDGE,"E109.MirrorCS"),sQuery(id+"F13.wireOp",EDGE,"E110.trimOffspring"),sQuery(id+"F13.wireOp",EDGE,"E111.top"),sQuery(id+"F13.wireOp",EDGE,"E111.left"),sQuery(id+"F13.wireOp",EDGE,"E111.right")])],"isStart":false});
            var sketch = newSketch(context, id + "F16", { "sketchPlane" : qUnion([Q0])});
            skPoint(sketch, "E126", {"position": v(0, -263.16) * mm});
            skPoint(sketch, "E126.positionSnap0", {"position": v(0, -293.16) * mm});
            skArc(sketch, "E127", {"start": v(3.5, -258.16) * mm, "mid": v(0, -254.66) * mm, "end": v(-3.5, -258.16) * mm});
            skArc(sketch, "E128", {"start": v(-3.5, -268.16) * mm, "mid": v(0, -271.66) * mm, "end": v(3.5, -268.16) * mm});
            skLineSegment(sketch, "E129", {"start": v(0, -268.16) * mm, "end": v(0, -258.16) * mm, "construction": true});
            skLineSegment(sketch, "E130", {"start": v(3.5, -258.16) * mm, "end": v(3.5, -268.16) * mm});
            skLineSegment(sketch, "E131", {"start": v(-3.5, -258.16) * mm, "end": v(-3.5, -268.16) * mm});
            skLineSegment(sketch, "E132", {"start": v(0, -301.11) * mm, "end": v(0, -224.38) * mm, "construction": true});
            skPoint(sketch, "E133", {"position": v(-32.5, -245.16) * mm});
            skPoint(sketch, "E134", {"position": v(32.5, -245.16) * mm});
            skPoint(sketch, "E135", {"position": v(32.5, -281.16) * mm});
            skPoint(sketch, "E136", {"position": v(-32.5, -281.16) * mm});
            skLineSegment(sketch, "E137", {"start": v(-32.5, -240.16) * mm, "end": v(-32.5, -250.16) * mm, "construction": true});
            skLineSegment(sketch, "E138", {"start": v(45.28, -263.16) * mm, "end": v(-51.7, -263.16) * mm, "construction": true});
            skLineSegment(sketch, "E139.MirrorCS", {"start": v(-65, -301.11) * mm, "end": v(-65, -224.38) * mm, "construction": true});
            skLineSegment(sketch, "E140.MirrorCS", {"start": v(32.5, -240.16) * mm, "end": v(32.5, -250.16) * mm, "construction": true});
            skLineSegment(sketch, "E141.MirrorCS", {"start": v(-32.5, -286.16) * mm, "end": v(-32.5, -276.16) * mm, "construction": true});
            skLineSegment(sketch, "E142.MirrorCS", {"start": v(32.5, -286.16) * mm, "end": v(32.5, -276.16) * mm, "construction": true});
            skArc(sketch, "E143.0.startCap", {"start": v(-34.5, -240.16) * mm, "mid": v(-32.5, -238.16) * mm, "end": v(-30.5, -240.16) * mm});
            skArc(sketch, "E143.0.endCap", {"start": v(-30.5, -250.16) * mm, "mid": v(-32.5, -252.16) * mm, "end": v(-34.5, -250.16) * mm});
            skLineSegment(sketch, "E143.0.left", {"start": v(-30.5, -240.16) * mm, "end": v(-30.5, -250.16) * mm});
            skLineSegment(sketch, "E143.0.right", {"start": v(-34.5, -240.16) * mm, "end": v(-34.5, -250.16) * mm});
            skArc(sketch, "E143.1.startCap", {"start": v(30.5, -240.16) * mm, "mid": v(32.5, -238.16) * mm, "end": v(34.5, -240.16) * mm});
            skArc(sketch, "E143.1.endCap", {"start": v(34.5, -250.16) * mm, "mid": v(32.5, -252.16) * mm, "end": v(30.5, -250.16) * mm});
            skLineSegment(sketch, "E143.1.left", {"start": v(34.5, -240.16) * mm, "end": v(34.5, -250.16) * mm});
            skLineSegment(sketch, "E143.1.right", {"start": v(30.5, -240.16) * mm, "end": v(30.5, -250.16) * mm});
            skArc(sketch, "E143.2.startCap", {"start": v(-30.5, -286.16) * mm, "mid": v(-32.5, -288.16) * mm, "end": v(-34.5, -286.16) * mm});
            skArc(sketch, "E143.2.endCap", {"start": v(-34.5, -276.16) * mm, "mid": v(-32.5, -274.16) * mm, "end": v(-30.5, -276.16) * mm});
            skLineSegment(sketch, "E143.2.left", {"start": v(-34.5, -286.16) * mm, "end": v(-34.5, -276.16) * mm});
            skLineSegment(sketch, "E143.2.right", {"start": v(-30.5, -286.16) * mm, "end": v(-30.5, -276.16) * mm});
            skArc(sketch, "E143.3.startCap", {"start": v(34.5, -286.16) * mm, "mid": v(32.5, -288.16) * mm, "end": v(30.5, -286.16) * mm});
            skArc(sketch, "E143.3.endCap", {"start": v(30.5, -276.16) * mm, "mid": v(32.5, -274.16) * mm, "end": v(34.5, -276.16) * mm});
            skLineSegment(sketch, "E143.3.left", {"start": v(30.5, -286.16) * mm, "end": v(30.5, -276.16) * mm});
            skLineSegment(sketch, "E143.3.right", {"start": v(34.5, -286.16) * mm, "end": v(34.5, -276.16) * mm});
            skSolve(sketch);
        }
        {
            var Q0;
            Q0=makeQuery(id+"F16.imprint","IMPRINT",FACE,{"disambiguationData":[TD([[makeQuery(id+"F16.imprint","IMPRINT",EDGE,{"derivedFrom":sQuery(id+"F16.wireOp",EDGE,"E127")}),1.0]])]});
            var Q1;
            Q1=makeQuery(id+"F16.imprint","IMPRINT",FACE,{"disambiguationData":[TD([[makeQuery(id+"F16.imprint","IMPRINT",EDGE,{"derivedFrom":sQuery(id+"F16.wireOp",EDGE,"E143.0.startCap")}),-1.0]])]});
            var Q2;
            Q2=makeQuery(id+"F16.imprint","IMPRINT",FACE,{"disambiguationData":[TD([[makeQuery(id+"F16.imprint","IMPRINT",EDGE,{"derivedFrom":sQuery(id+"F16.wireOp",EDGE,"E143.1.startCap")}),-1.0]])]});
            var Q3;
            Q3=makeQuery(id+"F16.imprint","IMPRINT",FACE,{"disambiguationData":[TD([[makeQuery(id+"F16.imprint","IMPRINT",EDGE,{"derivedFrom":sQuery(id+"F16.wireOp",EDGE,"E143.3.startCap")}),-1.0]])]});
            var Q4;
            Q4=makeQuery(id+"F16.imprint","IMPRINT",FACE,{"disambiguationData":[TD([[makeQuery(id+"F16.imprint","IMPRINT",EDGE,{"derivedFrom":sQuery(id+"F16.wireOp",EDGE,"E143.2.startCap")}),-1.0]])]});
            extrude(context, id + "F17", {"entities" : qUnion([Q0, Q1, Q2, Q3, Q4]), "operationType" : NewBodyOperationType.REMOVE, "oppositeDirection" : true, "depth" : 5 * mm, "offsetDistance" : 25 * mm});
        }
        {
            var Q0;
            Q0=qCreatedBy(makeId("Top.planeOp"),FACE);
            var sketch = newSketch(context, id + "F18", { "sketchPlane" : qUnion([Q0])});
            skLineSegment(sketch, "E144", {"start": v(0, -302.54) * mm, "end": v(0, -375.85) * mm, "construction": true});
            skLineSegment(sketch, "E145", {"start": v(-73.22, -339.2) * mm, "end": v(73.22, -339.2) * mm, "construction": true});
            skPoint(sketch, "E146", {"position": v(0, -339.2) * mm});
            skLineSegment(sketch, "E147.bottom", {"start": v(-50, -314.2) * mm, "end": v(50, -314.2) * mm});
            skLineSegment(sketch, "E147.top", {"start": v(-50, -364.2) * mm, "end": v(50, -364.2) * mm});
            skLineSegment(sketch, "E147.left", {"start": v(-50, -314.2) * mm, "end": v(-50, -364.2) * mm});
            skLineSegment(sketch, "E147.right", {"start": v(50, -314.2) * mm, "end": v(50, -364.2) * mm});
            skSolve(sketch);
        }
        {
            var Q0;
            Q0=makeQuery(id+"F18.imprint","IMPRINT",FACE,{"disambiguationData":[TD([[makeQuery(id+"F18.imprint","IMPRINT",EDGE,{"derivedFrom":sQuery(id+"F18.wireOp",EDGE,"E147.bottom")}),-1.0]])]});
            extrude(context, id + "F19", {"entities" : qUnion([Q0]), "depth" : 5 * mm, "offsetDistance" : 25 * mm});
        }
        {
            var Q0;
            Q0=makeQuery(id+"F19.opExtrude","SWEPT_EDGE",EDGE,{"disambiguationData":[OSD([sQuery(id+"F18.wireOp",EDGE,"E147.top"),sQuery(id+"F18.wireOp",EDGE,"E147.left")])]});
            var Q1;
            Q1=makeQuery(id+"F19.opExtrude","SWEPT_EDGE",EDGE,{"disambiguationData":[OSD([sQuery(id+"F18.wireOp",EDGE,"E147.top"),sQuery(id+"F18.wireOp",EDGE,"E147.right")])]});
            var Q2;
            Q2=makeQuery(id+"F19.opExtrude","SWEPT_EDGE",EDGE,{"disambiguationData":[OSD([sQuery(id+"F18.wireOp",EDGE,"E147.bottom"),sQuery(id+"F18.wireOp",EDGE,"E147.right")])]});
            var Q3;
            Q3=makeQuery(id+"F19.opExtrude","SWEPT_EDGE",EDGE,{"disambiguationData":[OSD([sQuery(id+"F18.wireOp",EDGE,"E147.bottom"),sQuery(id+"F18.wireOp",EDGE,"E147.left")])]});
            fillet(context, id + "F20", {"entities" : qUnion([Q0, Q1, Q2, Q3]), "radius" : 5 * mm, "tangentPropagation" : true, "allowEdgeOverflow" : false});
        }
        {
            var Q0;
            Q0=makeQuery(id+"F19.opExtrude","CAP_FACE",FACE,{"disambiguationData":[OSD([sQuery(id+"F18.wireOp",EDGE,"E147.bottom"),sQuery(id+"F18.wireOp",EDGE,"E147.top"),sQuery(id+"F18.wireOp",EDGE,"E147.left"),sQuery(id+"F18.wireOp",EDGE,"E147.right")])],"isStart":false});
            var sketch = newSketch(context, id + "F21", { "sketchPlane" : qUnion([Q0])});
            skLineSegment(sketch, "E148", {"start": v(0, -314.2) * mm, "end": v(0, -364.2) * mm, "construction": true});
            skPoint(sketch, "E149", {"position": v(0, -339.2) * mm});
            skSolve(sketch);
        }
        {
            var Q0;
            Q0=sQuery(id+"F21.wireOp",VERTEX,"E149");
            var Q1;
            Q1=makeQuery(id+"F19.opExtrude","SWEPT_BODY",BODY,{"disambiguationData":[OSD([sQuery(id+"F18.wireOp",EDGE,"E147.bottom"),sQuery(id+"F18.wireOp",EDGE,"E147.top"),sQuery(id+"F18.wireOp",EDGE,"E147.left"),sQuery(id+"F18.wireOp",EDGE,"E147.right")])]});
            hole(context, id + "F22", {"style" : HoleStyle.SIMPLE, "endStyle" : HoleEndStyle.THROUGH, "holeDiameter" : 7 * mm, "majorDiameter" : 5 * mm, "isTappedThrough" : true, "tappedDepth" : 12 * mm, "tapClearance" : 3, "locations" : qUnion([Q0]), "scope" : qUnion([Q1])});
        }
        {
            var Q0;
            Q0=makeQuery(id+"F19.opExtrude","CAP_FACE",FACE,{"disambiguationData":[OSD([sQuery(id+"F18.wireOp",EDGE,"E147.bottom"),sQuery(id+"F18.wireOp",EDGE,"E147.top"),sQuery(id+"F18.wireOp",EDGE,"E147.left"),sQuery(id+"F18.wireOp",EDGE,"E147.right")])],"isStart":false});
            var sketch = newSketch(context, id + "F23", { "sketchPlane" : qUnion([Q0])});
            skPoint(sketch, "E150", {"position": v(0, -339.2) * mm});
            skLineSegment(sketch, "E151", {"start": v(76.22, -339.2) * mm, "end": v(-85.35, -339.2) * mm, "construction": true});
            skLineSegment(sketch, "E152", {"start": v(0, -298.02) * mm, "end": v(0, -380.37) * mm, "construction": true});
            skPoint(sketch, "E153", {"position": v(-32.5, -321.2) * mm});
            skPoint(sketch, "E154", {"position": v(32.5, -321.2) * mm});
            skPoint(sketch, "E155", {"position": v(32.5, -357.2) * mm});
            skPoint(sketch, "E156", {"position": v(-32.5, -357.2) * mm});
            skSolve(sketch);
        }
        {
            var Q0;
            Q0=sQuery(id+"F23.wireOp",VERTEX,"E153");
            var Q1;
            Q1=sQuery(id+"F23.wireOp",VERTEX,"E156");
            var Q2;
            Q2=sQuery(id+"F23.wireOp",VERTEX,"E155");
            var Q3;
            Q3=sQuery(id+"F23.wireOp",VERTEX,"E154");
            var Q4;
            Q4=makeQuery(id+"F19.opExtrude","SWEPT_BODY",BODY,{"disambiguationData":[OSD([sQuery(id+"F18.wireOp",EDGE,"E147.bottom"),sQuery(id+"F18.wireOp",EDGE,"E147.top"),sQuery(id+"F18.wireOp",EDGE,"E147.left"),sQuery(id+"F18.wireOp",EDGE,"E147.right")])]});
            hole(context, id + "F24", {"style" : HoleStyle.SIMPLE, "endStyle" : HoleEndStyle.THROUGH, "holeDiameter" : 4 * mm, "majorDiameter" : 5 * mm, "isTappedThrough" : true, "tappedDepth" : 12 * mm, "tapClearance" : 3, "locations" : qUnion([Q0, Q1, Q2, Q3]), "scope" : qUnion([Q4])});
        }
        {
            var Q0;
            Q0=makeQuery(id+"F1.opExtrude","CAP_FACE",FACE,{"disambiguationData":[OSD([sQuery(id+"F0.wireOp",EDGE,"E0.top"),sQuery(id+"F0.wireOp",EDGE,"E0.left"),sQuery(id+"F0.wireOp",EDGE,"E0.right"),sQuery(id+"F0.wireOp",EDGE,"E3"),sQuery(id+"F0.wireOp",EDGE,"E4"),sQuery(id+"F0.wireOp",EDGE,"E5"),sQuery(id+"F0.wireOp",EDGE,"E6.bottom"),sQuery(id+"F0.wireOp",EDGE,"E6.top"),sQuery(id+"F0.wireOp",EDGE,"E6.right"),sQuery(id+"F0.wireOp",EDGE,"E7.MirrorCS"),sQuery(id+"F0.wireOp",EDGE,"E8.MirrorCS"),sQuery(id+"F0.wireOp",EDGE,"E9.MirrorCS"),sQuery(id+"F0.wireOp",EDGE,"E10.bottom"),sQuery(id+"F0.wireOp",EDGE,"E10.top"),sQuery(id+"F0.wireOp",EDGE,"E10.right"),sQuery(id+"F0.wireOp",EDGE,"E11.bottom"),sQuery(id+"F0.wireOp",EDGE,"E11.top"),sQuery(id+"F0.wireOp",EDGE,"E11.right"),sQuery(id+"F0.wireOp",EDGE,"E12.bottom"),sQuery(id+"F0.wireOp",EDGE,"E12.top"),sQuery(id+"F0.wireOp",EDGE,"E12.right"),sQuery(id+"F0.wireOp",EDGE,"E13.MirrorCS"),sQuery(id+"F0.wireOp",EDGE,"E14.MirrorCS"),sQuery(id+"F0.wireOp",EDGE,"E15.MirrorCS"),sQuery(id+"F0.wireOp",EDGE,"E16.MirrorCS"),sQuery(id+"F0.wireOp",EDGE,"E17.MirrorCS"),sQuery(id+"F0.wireOp",EDGE,"E18.MirrorCS"),sQuery(id+"F0.wireOp",EDGE,"E19.MirrorCS"),sQuery(id+"F0.wireOp",EDGE,"E20.MirrorCS"),sQuery(id+"F0.wireOp",EDGE,"E21.MirrorCS"),sQuery(id+"F0.wireOp",EDGE,"E22.trimOffspring"),sQuery(id+"F0.wireOp",EDGE,"E23.trimOffspring"),sQuery(id+"F0.wireOp",EDGE,"E24.trimOffspring"),sQuery(id+"F0.wireOp",EDGE,"E25.trimOffspring"),sQuery(id+"F0.wireOp",EDGE,"E26.trimOffspring"),sQuery(id+"F0.wireOp",EDGE,"E27.trimOffspring"),sQuery(id+"F0.wireOp",EDGE,"E28.bottom"),sQuery(id+"F0.wireOp",EDGE,"E28.top"),sQuery(id+"F0.wireOp",EDGE,"E28.left"),sQuery(id+"F0.wireOp",EDGE,"E28.right")])],"isStart":false});
            var sketch = newSketch(context, id + "F25", { "sketchPlane" : qUnion([Q0])});
            skLineSegment(sketch, "E157", {"start": v(0, -64.55) * mm, "end": v(0, 105.2) * mm, "construction": true});
            skPoint(sketch, "E158", {"position": v(-58, 65) * mm});
            skPoint(sketch, "E158.positionSnap0", {"position": v(-60.5, 65) * mm});
            skPoint(sketch, "E159.MirrorP", {"position": v(58, 65) * mm});
            skPoint(sketch, "E160", {"position": v(-58, -100) * mm});
            skPoint(sketch, "E160.positionSnap0", {"position": v(-60.5, -100) * mm});
            skPoint(sketch, "E161.MirrorP", {"position": v(58, -100) * mm});
            skPoint(sketch, "E162", {"position": v(-58, -45) * mm});
            skPoint(sketch, "E162.positionSnap0", {"position": v(-60.5, -45) * mm});
            skPoint(sketch, "E163.MirrorP", {"position": v(58, -45) * mm});
            skSolve(sketch);
        }
        {
            var Q0;
            Q0=sQuery(id+"F25.wireOp",VERTEX,"E158");
            var Q1;
            Q1=sQuery(id+"F25.wireOp",VERTEX,"E159.MirrorP");
            var Q2;
            Q2=sQuery(id+"F25.wireOp",VERTEX,"E160");
            var Q3;
            Q3=sQuery(id+"F25.wireOp",VERTEX,"E161.MirrorP");
            var Q4;
            Q4=sQuery(id+"F25.wireOp",VERTEX,"E162");
            var Q5;
            Q5=sQuery(id+"F25.wireOp",VERTEX,"E163.MirrorP");
            var Q6;
            Q6=makeQuery(id+"F1.opExtrude","SWEPT_BODY",BODY,{"disambiguationData":[OSD([sQuery(id+"F0.wireOp",EDGE,"E0.top"),sQuery(id+"F0.wireOp",EDGE,"E0.left"),sQuery(id+"F0.wireOp",EDGE,"E0.right"),sQuery(id+"F0.wireOp",EDGE,"E3"),sQuery(id+"F0.wireOp",EDGE,"E4"),sQuery(id+"F0.wireOp",EDGE,"E5"),sQuery(id+"F0.wireOp",EDGE,"E6.bottom"),sQuery(id+"F0.wireOp",EDGE,"E6.top"),sQuery(id+"F0.wireOp",EDGE,"E6.right"),sQuery(id+"F0.wireOp",EDGE,"E7.MirrorCS"),sQuery(id+"F0.wireOp",EDGE,"E8.MirrorCS"),sQuery(id+"F0.wireOp",EDGE,"E9.MirrorCS"),sQuery(id+"F0.wireOp",EDGE,"E10.bottom"),sQuery(id+"F0.wireOp",EDGE,"E10.top"),sQuery(id+"F0.wireOp",EDGE,"E10.right"),sQuery(id+"F0.wireOp",EDGE,"E11.bottom"),sQuery(id+"F0.wireOp",EDGE,"E11.top"),sQuery(id+"F0.wireOp",EDGE,"E11.right"),sQuery(id+"F0.wireOp",EDGE,"E12.bottom"),sQuery(id+"F0.wireOp",EDGE,"E12.top"),sQuery(id+"F0.wireOp",EDGE,"E12.right"),sQuery(id+"F0.wireOp",EDGE,"E13.MirrorCS"),sQuery(id+"F0.wireOp",EDGE,"E14.MirrorCS"),sQuery(id+"F0.wireOp",EDGE,"E15.MirrorCS"),sQuery(id+"F0.wireOp",EDGE,"E16.MirrorCS"),sQuery(id+"F0.wireOp",EDGE,"E17.MirrorCS"),sQuery(id+"F0.wireOp",EDGE,"E18.MirrorCS"),sQuery(id+"F0.wireOp",EDGE,"E19.MirrorCS"),sQuery(id+"F0.wireOp",EDGE,"E20.MirrorCS"),sQuery(id+"F0.wireOp",EDGE,"E21.MirrorCS"),sQuery(id+"F0.wireOp",EDGE,"E22.trimOffspring"),sQuery(id+"F0.wireOp",EDGE,"E23.trimOffspring"),sQuery(id+"F0.wireOp",EDGE,"E24.trimOffspring"),sQuery(id+"F0.wireOp",EDGE,"E25.trimOffspring"),sQuery(id+"F0.wireOp",EDGE,"E26.trimOffspring"),sQuery(id+"F0.wireOp",EDGE,"E27.trimOffspring"),sQuery(id+"F0.wireOp",EDGE,"E28.bottom"),sQuery(id+"F0.wireOp",EDGE,"E28.top"),sQuery(id+"F0.wireOp",EDGE,"E28.left"),sQuery(id+"F0.wireOp",EDGE,"E28.right")])]});
            hole(context, id + "F26", {"style" : HoleStyle.SIMPLE, "endStyle" : HoleEndStyle.THROUGH, "holeDiameter" : 2 * mm, "majorDiameter" : 5 * mm, "isTappedThrough" : true, "tappedDepth" : 12 * mm, "tapClearance" : 3, "locations" : qUnion([Q0, Q1, Q2, Q3, Q4, Q5]), "scope" : qUnion([Q6])});
        }
    });
